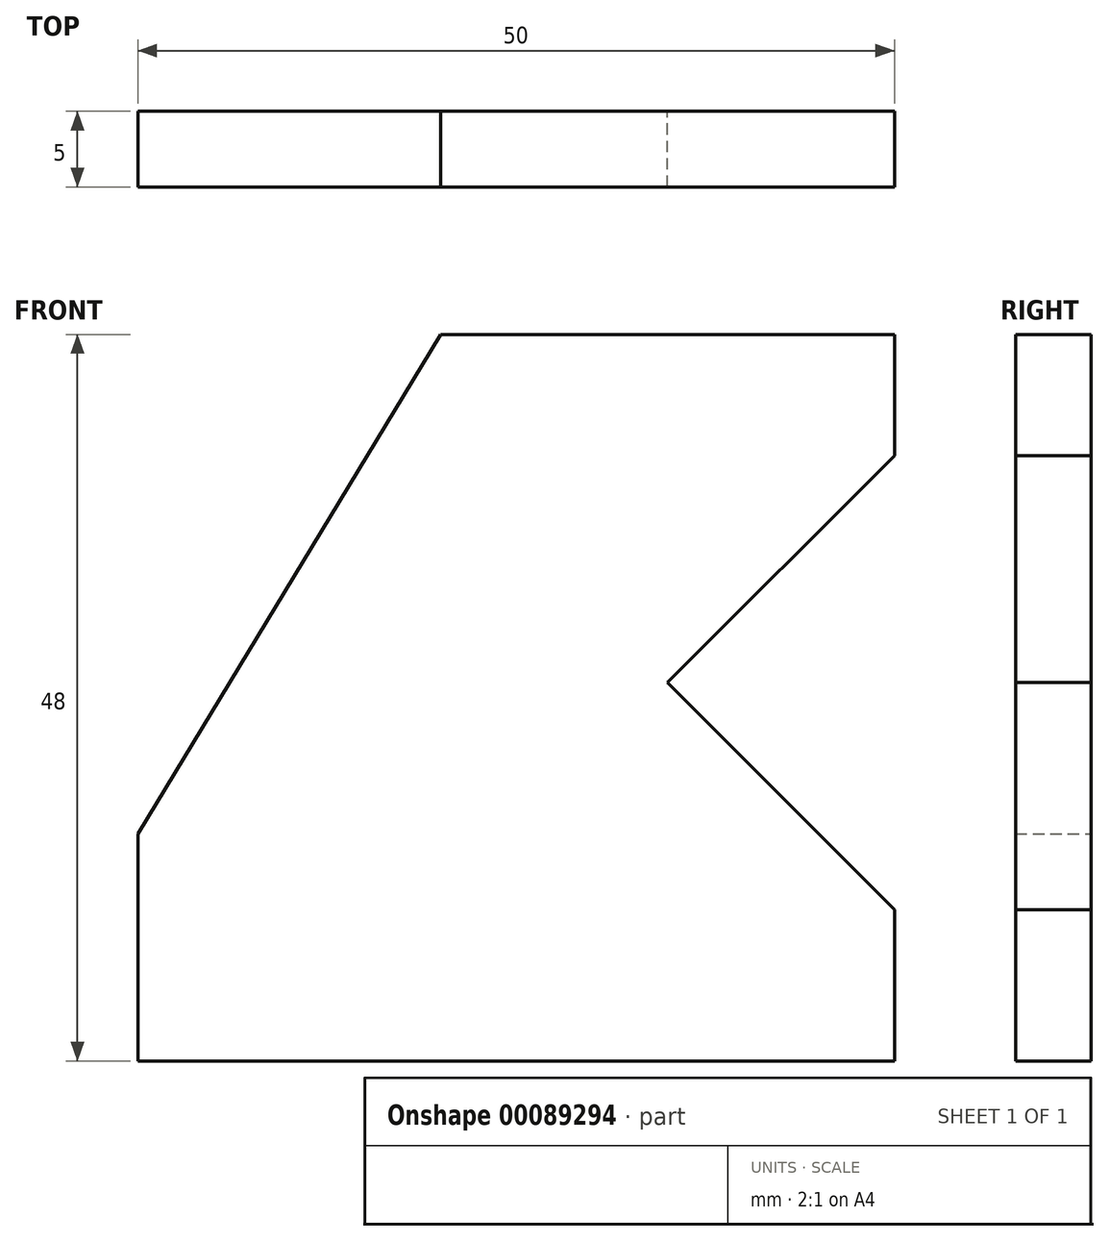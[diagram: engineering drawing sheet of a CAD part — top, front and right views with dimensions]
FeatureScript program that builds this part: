
annotation { "Feature Type Name" : "Feature", "Feature Type Description" : "" }
export const myFeature = defineFeature(function(context is Context, id is Id, definition is map)
    precondition{}
    {
        {
            var Q0;
            Q0=qCreatedBy(makeId("Front.planeOp"),FACE);
            var sketch = newSketch(context, id + "F0", { "sketchPlane" : qUnion([Q0])});
            skLineSegment(sketch, "E0", {"start": v(0, 0) * mm, "end": v(15, 15) * mm});
            skLineSegment(sketch, "E1", {"start": v(15, 15) * mm, "end": v(15, 23) * mm});
            skLineSegment(sketch, "E2", {"start": v(15, 23) * mm, "end": v(-15, 23) * mm});
            skLineSegment(sketch, "E3", {"start": v(-15, 23) * mm, "end": v(-35, -10) * mm});
            skLineSegment(sketch, "E4", {"start": v(-35, -10) * mm, "end": v(-35, -25) * mm});
            skLineSegment(sketch, "E5", {"start": v(-35, -25) * mm, "end": v(15, -25) * mm});
            skLineSegment(sketch, "E6", {"start": v(15, -25) * mm, "end": v(15, -15) * mm});
            skLineSegment(sketch, "E7", {"start": v(15, -15) * mm, "end": v(0, 0) * mm});
            skSolve(sketch);
        }
        {
            var Q0;
            Q0 = qSketchRegion(id + "F0", true);
            extrude(context, id + "F1", {"entities" : qUnion([Q0]), "depth" : 5 * mm});
        }
    });
